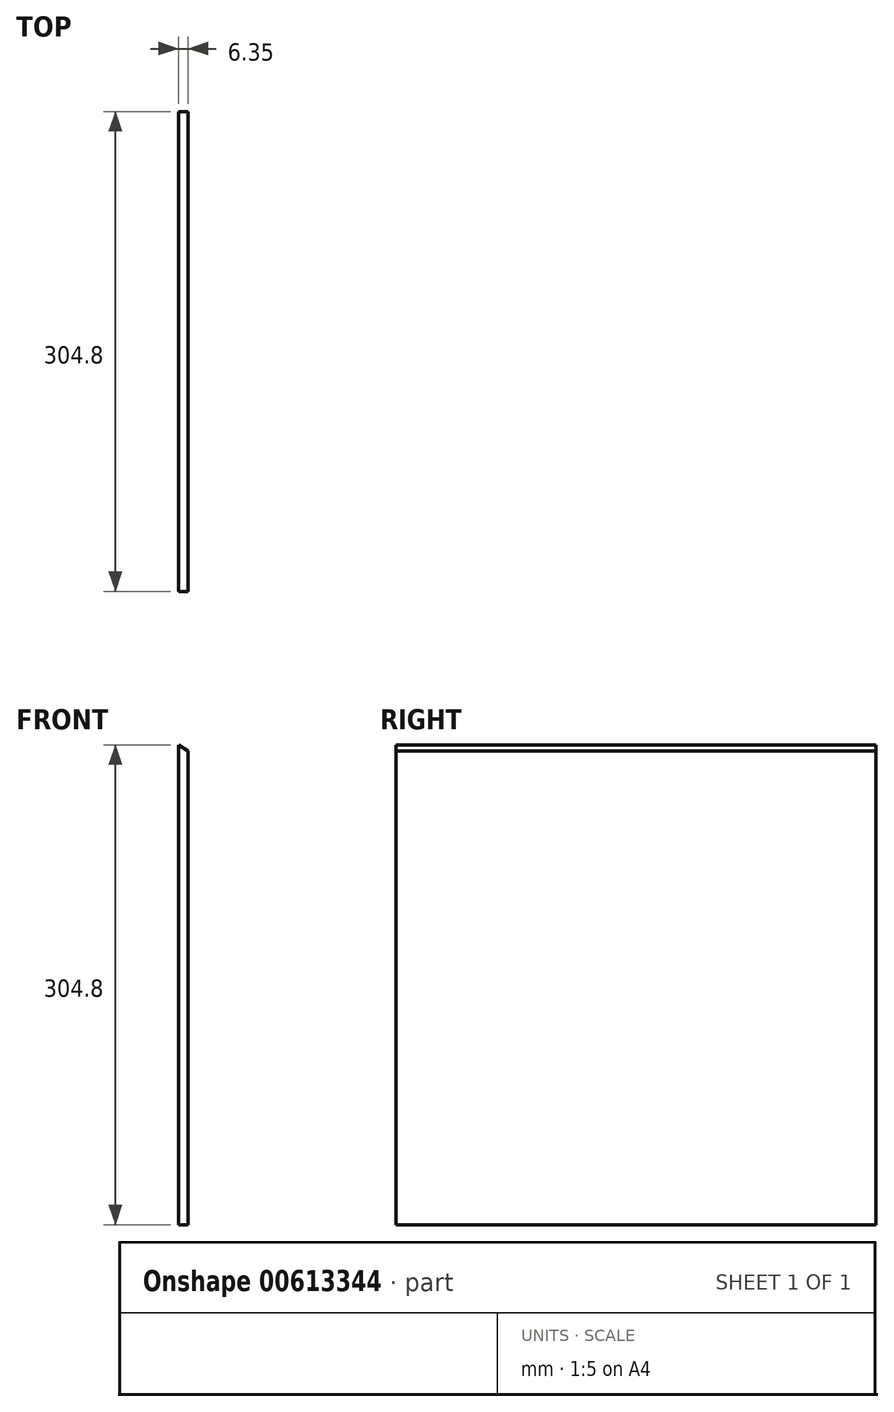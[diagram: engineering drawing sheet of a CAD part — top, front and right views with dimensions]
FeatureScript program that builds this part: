
annotation { "Feature Type Name" : "Feature", "Feature Type Description" : "" }
export const myFeature = defineFeature(function(context is Context, id is Id, definition is map)
    precondition{}
    {
        {
            var Q0;
            Q0=qCreatedBy(makeId("Front.planeOp"),FACE);
            var sketch = newSketch(context, id + "F0", { "sketchPlane" : qUnion([Q0])});
            skLineSegment(sketch, "E0.top", {"start": v(3.18, -152.4) * mm, "end": v(-3.17, -152.4) * mm});
            skLineSegment(sketch, "E0.left", {"start": v(3.17, 148.37) * mm, "end": v(3.18, -152.4) * mm});
            skLineSegment(sketch, "E0.right", {"start": v(-3.18, 152.4) * mm, "end": v(-3.17, -152.4) * mm});
            skPoint(sketch, "E0.middle", {"position": v(0, 0) * mm});
            skLineSegment(sketch, "E1", {"start": v(-3.18, 152.4) * mm, "end": v(3.17, 148.37) * mm});
            skPoint(sketch, "E2.orphan", {"position": v(3.17, 152.4) * mm});
            skSolve(sketch);
        }
        {
            var Q0;
            Q0 = qSketchRegion(id + "F0", true);
            extrude(context, id + "F1", {"entities" : qUnion([Q0]), "depth" : 304.8 * mm, "offsetDistance" : 25.4 * mm});
        }
    });
